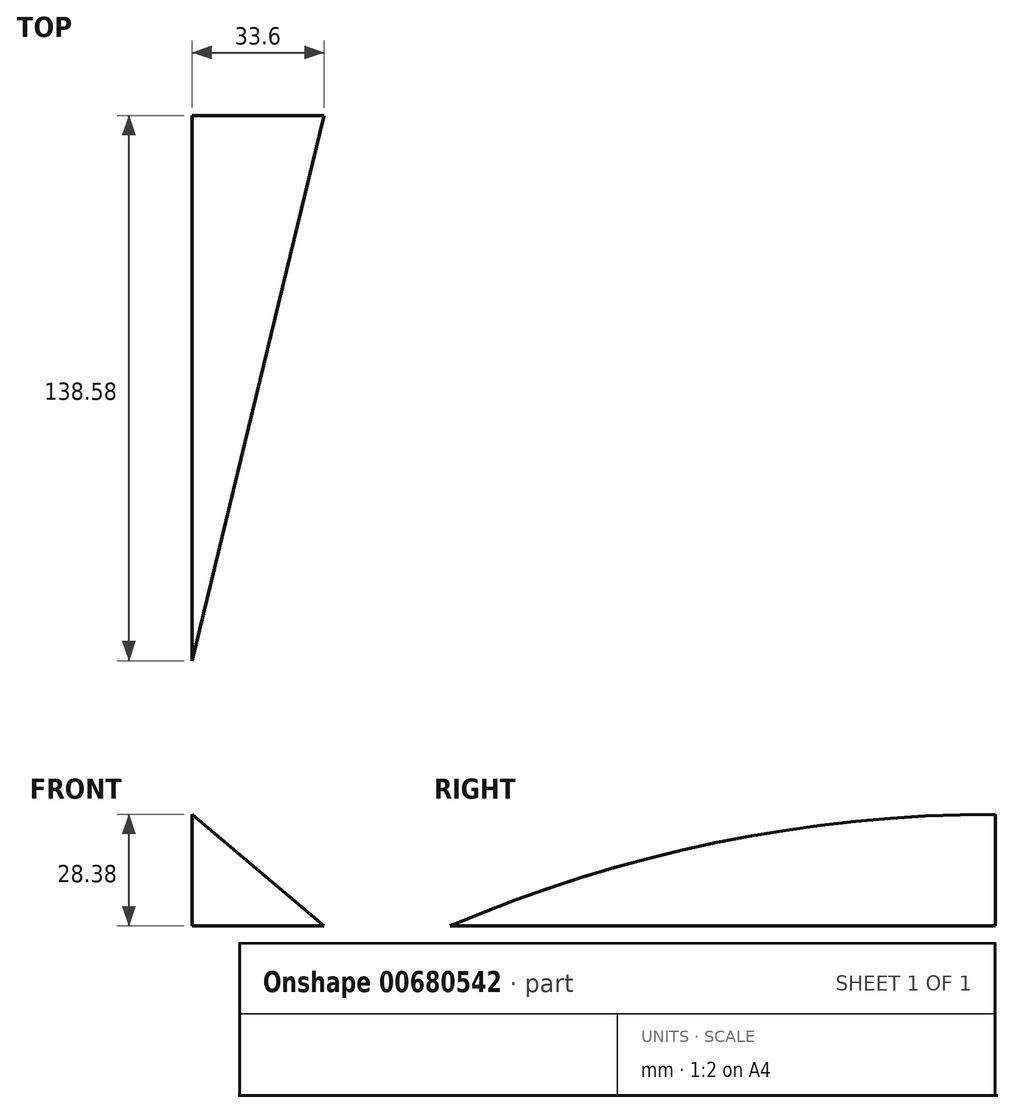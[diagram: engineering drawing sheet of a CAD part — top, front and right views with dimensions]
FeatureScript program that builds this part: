
annotation { "Feature Type Name" : "Feature", "Feature Type Description" : "" }
export const myFeature = defineFeature(function(context is Context, id is Id, definition is map)
    precondition{}
    {
        {
            var Q0;
            Q0=qCreatedBy(makeId("Right.planeOp"),FACE);
            var sketch = newSketch(context, id + "F0", { "sketchPlane" : qUnion([Q0])});
            skLineSegment(sketch, "E0", {"start": v(57.08, 28.38) * mm, "end": v(21.78, 28.38) * mm, "construction": true});
            skArc(sketch, "E1", {"start": v(21.78, 28.38) * mm, "mid": v(-48.95, 21.2) * mm, "end": v(-116.8, 0) * mm});
            skLineSegment(sketch, "E2", {"start": v(-116.8, 0) * mm, "end": v(21.78, 0) * mm});
            skLineSegment(sketch, "E3", {"start": v(21.78, 0) * mm, "end": v(21.78, 28.38) * mm});
            skSolve(sketch);
        }
        {
            var Q0;
            Q0=qCreatedBy(makeId("Top.planeOp"),FACE);
            var sketch = newSketch(context, id + "F1", { "sketchPlane" : qUnion([Q0])});
            skLineSegment(sketch, "E4", {"start": v(0, 21.78) * mm, "end": v(33.6, 21.78) * mm});
            skLineSegment(sketch, "E5", {"start": v(33.6, 21.78) * mm, "end": v(0, -116.8) * mm});
            skLineSegment(sketch, "E6", {"start": v(0, -116.8) * mm, "end": v(0, 21.78) * mm});
            skSolve(sketch);
        }
        {
            var Q0;
            Q0=sQuery(id+"F0.wireOp",EDGE,"E1");
            var Q1;
            Q1=sQuery(id+"F1.wireOp",EDGE,"E5");
            loft(context, id + "F2", {"bodyType" : ToolBodyType.SURFACE, "wireProfilesArray" : [{ "wireProfileEntities" : qUnion([Q0]) }, { "wireProfileEntities" : qUnion([Q1]) }]});
        }
        {
            var Q0;
            Q0 = qSketchRegion(id + "F1", true);
            var Q1;
            Q1=makeQuery(id+"F2.opLoft","SWEPT_BODY",BODY,{"disambiguationData":[OSD([sQuery(id+"F0.wireOp",EDGE,"E1"),sQuery(id+"F1.wireOp",EDGE,"E5")])]});
            loft(context, id + "F3", {"sheetProfilesArray" : [{ "sheetProfileEntities" : qUnion([Q0]) }, { "sheetProfileEntities" : qUnion([Q1]) }]});
        }
    });
